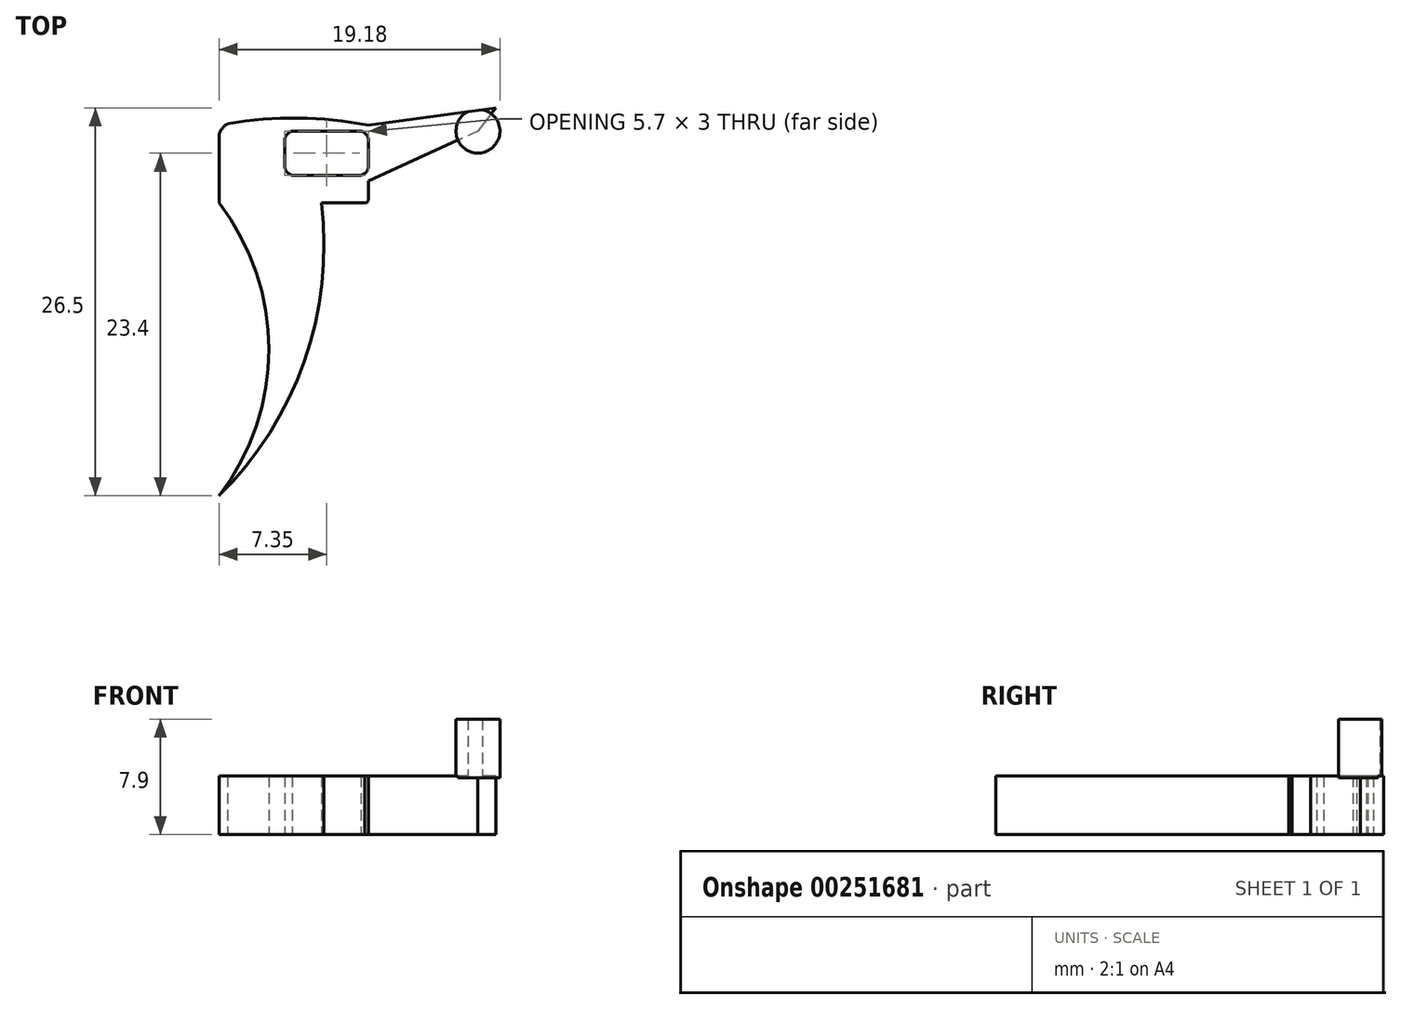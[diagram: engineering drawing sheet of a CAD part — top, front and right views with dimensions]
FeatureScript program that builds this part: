
annotation { "Feature Type Name" : "Feature", "Feature Type Description" : "" }
export const myFeature = defineFeature(function(context is Context, id is Id, definition is map)
    precondition{}
    {
        {
            var Q0;
            Q0=qCreatedBy(makeId("Top.planeOp"),FACE);
            var sketch = newSketch(context, id + "F0", { "sketchPlane" : qUnion([Q0])});
            skLineSegment(sketch, "E0", {"start": v(-0.23, 0) * mm, "end": v(-3.2, 0) * mm});
            skLineSegment(sketch, "E1", {"start": v(0, 0.23) * mm, "end": v(0, 1.5) * mm});
            skLineSegment(sketch, "E2", {"start": v(-10.2, 0) * mm, "end": v(-10.2, 4.65) * mm});
            skPoint(sketch, "E3", {"position": v(0, 1.5) * mm});
            skLineSegment(sketch, "E4", {"start": v(8.7, 6.5) * mm, "end": v(0, 5.3) * mm});
            skLineSegment(sketch, "E5", {"start": v(8.7, 6.5) * mm, "end": v(7.48, 4.9) * mm});
            skLineSegment(sketch, "E6", {"start": v(7.48, 4.9) * mm, "end": v(0, 1.5) * mm});
            skArc(sketch, "E7", {"start": v(-10.2, -20) * mm, "mid": v(-6.8, -10) * mm, "end": v(-10.2, 0) * mm});
            skPoint(sketch, "E8.start.orphan", {"position": v(-10.2, -10) * mm});
            skPoint(sketch, "E9", {"position": v(-3.2, 0) * mm});
            skArc(sketch, "E10", {"start": v(-10.2, -20) * mm, "mid": v(-4.37, -10.82) * mm, "end": v(-3.2, 0) * mm});
            skPoint(sketch, "E11.endSnap0", {"position": v(-2.85, 4.15) * mm});
            skLineSegment(sketch, "E12", {"start": v(-2.85, 1.9) * mm, "end": v(-0.5, 1.9) * mm});
            skLineSegment(sketch, "E13", {"start": v(-5.7, 3.4) * mm, "end": v(-5.7, 2.4) * mm});
            skLineSegment(sketch, "E14", {"start": v(-2.85, 1.9) * mm, "end": v(-5.2, 1.9) * mm});
            skLineSegment(sketch, "E15", {"start": v(-5.7, 3.4) * mm, "end": v(-5.7, 4.4) * mm});
            skLineSegment(sketch, "E16", {"start": v(-2.85, 4.9) * mm, "end": v(-5.2, 4.9) * mm});
            skLineSegment(sketch, "E17", {"start": v(-5.2, 4.9) * mm, "end": v(-0.5, 4.9) * mm});
            skPoint(sketch, "E18.orphan", {"position": v(0, 3.4) * mm});
            skLineSegment(sketch, "E19", {"start": v(0, 2.4) * mm, "end": v(0, 4.4) * mm});
            skPoint(sketch, "E20", {"position": v(-0.5, 1.9) * mm});
            skPoint(sketch, "E21", {"position": v(0, 2.4) * mm});
            skArc(sketch, "E22", {"start": v(-0.5, 1.9) * mm, "mid": v(-0.18, 2.08) * mm, "end": v(0, 2.4) * mm});
            skPoint(sketch, "E23", {"position": v(-5.2, 1.9) * mm});
            skPoint(sketch, "E24", {"position": v(-5.7, 2.4) * mm});
            skPoint(sketch, "E25", {"position": v(-5.7, 4.4) * mm});
            skPoint(sketch, "E26", {"position": v(-5.2, 4.9) * mm});
            skPoint(sketch, "E27", {"position": v(-0.5, 4.9) * mm});
            skPoint(sketch, "E28", {"position": v(0, 4.4) * mm});
            skArc(sketch, "E29", {"start": v(-5.2, 4.9) * mm, "mid": v(-5.52, 4.72) * mm, "end": v(-5.7, 4.4) * mm});
            skArc(sketch, "E30", {"start": v(-5.7, 2.4) * mm, "mid": v(-5.52, 2.08) * mm, "end": v(-5.2, 1.9) * mm});
            skArc(sketch, "E31", {"start": v(0, 4.4) * mm, "mid": v(-0.18, 4.72) * mm, "end": v(-0.5, 4.9) * mm});
            skPoint(sketch, "E32.orphan", {"position": v(-5.7, 4.9) * mm});
            skPoint(sketch, "E33.end.orphan", {"position": v(0, 4.9) * mm});
            skPoint(sketch, "E34.start.orphan", {"position": v(-6.8, -10) * mm});
            skPoint(sketch, "E35", {"position": v(-0.25, 0) * mm});
            skPoint(sketch, "E36.end.orphan", {"position": v(0, 0.25) * mm});
            skPoint(sketch, "E37.start.orphan", {"position": v(0.14, 0) * mm});
            skArc(sketch, "E38", {"start": v(-0.25, 0) * mm, "mid": v(-0.07, 0.07) * mm, "end": v(0, 0.25) * mm});
            skPoint(sketch, "E39.orphan", {"position": v(0, 0) * mm});
            skArc(sketch, "E40", {"start": v(0, 5.3) * mm, "mid": v(-4.8, 5.8) * mm, "end": v(-9.6, 5.41) * mm});
            skPoint(sketch, "E41.start.orphan", {"position": v(-5.1, 5.3) * mm});
            skArc(sketch, "E42", {"start": v(-9.6, 5.41) * mm, "mid": v(-9.98, 5.09) * mm, "end": v(-10.2, 4.65) * mm});
            skPoint(sketch, "E43.start.orphan", {"position": v(-10.2, 5.3) * mm});
            skSolve(sketch);
        }
        {
            var Q0;
            Q0=makeQuery(id+"F0.imprint","IMPRINT",FACE,{"disambiguationData":[TD([[makeQuery(id+"F0.imprint","IMPRINT",EDGE,{"derivedFrom":sQuery(id+"F0.wireOp",EDGE,"E2")}),-1.0]])]});
            extrude(context, id + "F1", {"entities" : qUnion([Q0]), "depth" : 4 * mm});
        }
        {
            var Q0;
            Q0=qCreatedBy(makeId("Top.planeOp"),FACE);
            cPlane(context, id + "F2", {"entities" : qUnion([Q0]), "cplaneType" : CPlaneType.OFFSET, "offset" : 3.9 * mm, "width" : 150 * mm, "height" : 150 * mm});
        }
        {
            var Q0;
            Q0=qCreatedBy(id+"F2.planeOp",FACE);
            var sketch = newSketch(context, id + "F3", { "sketchPlane" : qUnion([Q0])});
            skArc(sketch, "E44", {"start": v(6.79, 6.24) * mm, "mid": v(7.69, 3.42) * mm, "end": v(7.8, 6.37) * mm});
            skPoint(sketch, "E45", {"position": v(6.79, 6.24) * mm});
            skPoint(sketch, "E46", {"position": v(7.8, 6.37) * mm});
            skLineSegment(sketch, "E47", {"start": v(7.8, 6.37) * mm, "end": v(6.79, 6.24) * mm});
            skSolve(sketch);
        }
        {
            var Q0;
            Q0=makeQuery(id+"F3.imprint","IMPRINT",FACE,{"disambiguationData":[TD([[makeQuery(id+"F3.imprint","IMPRINT",EDGE,{"derivedFrom":sQuery(id+"F3.wireOp",EDGE,"E44")}),1.0]])]});
            extrude(context, id + "F4", {"entities" : qUnion([Q0]), "operationType" : NewBodyOperationType.ADD, "depth" : 4 * mm});
        }
    });
